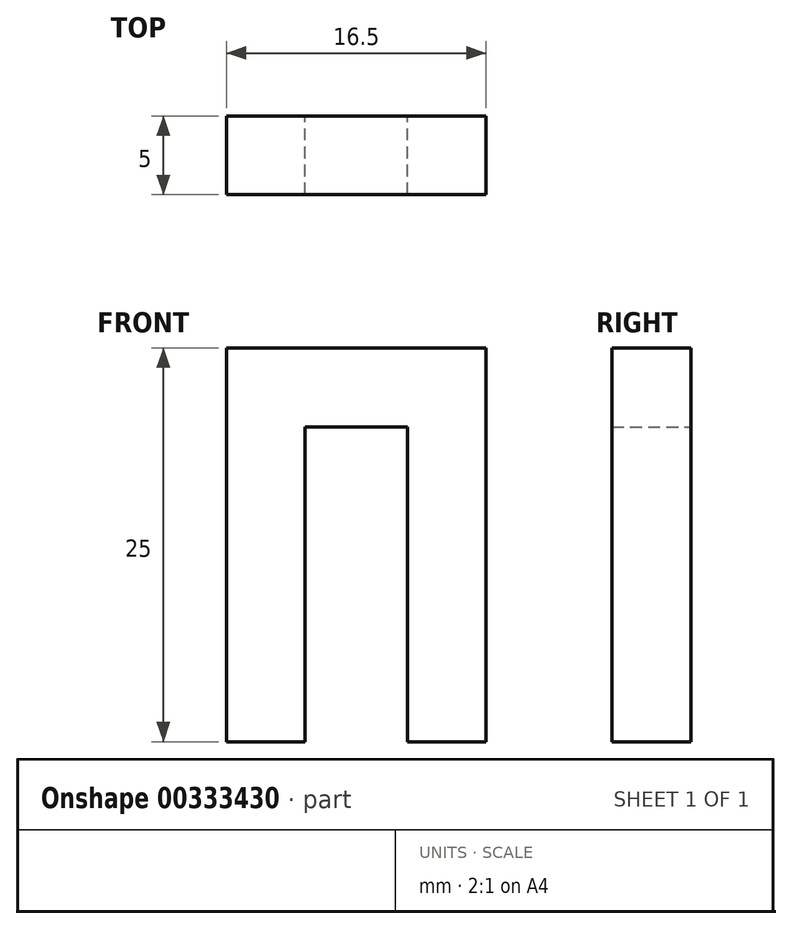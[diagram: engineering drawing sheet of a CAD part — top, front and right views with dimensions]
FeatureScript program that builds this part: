
annotation { "Feature Type Name" : "Feature", "Feature Type Description" : "" }
export const myFeature = defineFeature(function(context is Context, id is Id, definition is map)
    precondition{}
    {
        {
            var Q0;
            Q0=qCreatedBy(makeId("Front.planeOp"),FACE);
            var sketch = newSketch(context, id + "F0", { "sketchPlane" : qUnion([Q0])});
            skLineSegment(sketch, "E0", {"start": v(0, 0) * mm, "end": v(0, 20) * mm});
            skLineSegment(sketch, "E1", {"start": v(0, 20) * mm, "end": v(6.5, 20) * mm});
            skLineSegment(sketch, "E2", {"start": v(6.5, 20) * mm, "end": v(6.5, 0) * mm});
            skLineSegment(sketch, "E3.0", {"start": v(11.5, 25) * mm, "end": v(11.5, 0) * mm});
            skLineSegment(sketch, "E3.1", {"start": v(-5, 25) * mm, "end": v(11.5, 25) * mm});
            skLineSegment(sketch, "E3.2", {"start": v(-5, 0) * mm, "end": v(-5, 25) * mm});
            skLineSegment(sketch, "E4", {"start": v(-5, 0) * mm, "end": v(0, 0) * mm});
            skLineSegment(sketch, "E5", {"start": v(6.5, 0) * mm, "end": v(11.5, 0) * mm});
            skSolve(sketch);
        }
        {
            var Q0;
            Q0=makeQuery(id+"F0.imprint","IMPRINT",FACE,{"disambiguationData":[TD([[makeQuery(id+"F0.imprint","IMPRINT",EDGE,{"derivedFrom":sQuery(id+"F0.wireOp",EDGE,"E0")}),1.0]])]});
            extrude(context, id + "F1", {"entities" : qUnion([Q0]), "endBound" : BoundingType.SYMMETRIC, "depth" : 5 * mm});
        }
    });
